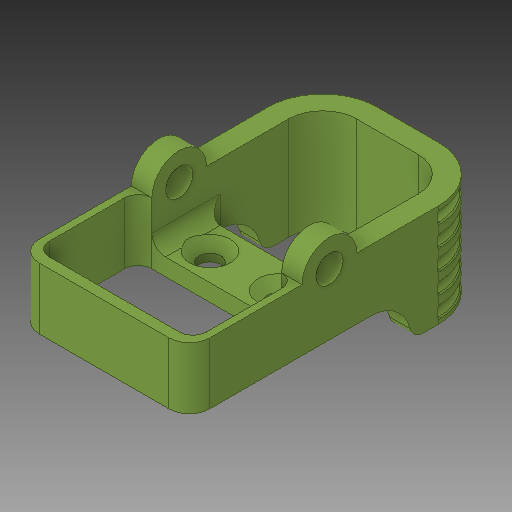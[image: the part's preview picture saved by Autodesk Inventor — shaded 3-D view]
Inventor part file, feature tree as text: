
AUTODESK INVENTOR PART (.ipt)
format: ipt  version: 2018 (Build 220112000, 112)  size: 946,688 bytes
history: native  units: mm
features: sketch x8, extrude x7, fillet x4, plane x2, projected_geometry x2, hole x1, sweep x1, pattern_linear x1
ambient origin geometry x8: Origin, YZ Plane, XZ Plane, XY Plane, X Axis, Y Axis, Z Axis, Center Point
bodies: Solid1 (feature_tree)
feature tree (26):
  extrude  "Extrusion1"  Depth=25.0mm
  extrude  "Extrusion2"  Depth=3.0mm
  sketch  "Sketch3"  dims[d4=15.0mm d5=0.0mm d6=15.0mm]
  extrude  "Extrusion3"  Depth=15.0mm
  extrude  "Extrusion4"  Depth=26.5mm
  extrude  "Extrusion5"  Depth=2.0mm
  hole  "Hole1"  [1 undecoded]
  extrude  "Extrusion6"  Depth=20.5mm
  extrude  "Extrusion7"  Depth=2.0mm
  plane  "Work Plane1"
  sketch  "Sketch7"  dims[d15=4.0mm d17=20.5mm]
  plane  "Work Plane2"
  sweep  "Sweep1"
  pattern_linear  "Rectangular Pattern1"  Spacing1=23.0mm  [1 undecoded]
  fillet  "Fillet1"  Radius=15.0mm
  fillet  "Fillet2"  Radius=1.0mm
  fillet  "Fillet3"  Radius=1.5mm
  fillet  "Fillet4"  Radius=3.0mm
  sketch  "Sketch1"  dims[d0=44.5mm d1=25.0mm]
  sketch  "Sketch2"  dims[d2=8.0mm d3=3.0mm]
  sketch  "Sketch4"  dims[d7=9.0mm d9=26.5mm]
  sketch  "Sketch5"  dims[d10=6.0mm d11=2.0mm]
  sketch  "Sketch6"  dims[d12=15.0mm d13=0.0mm d14=8.0mm]
  sketch  "Sketch8"  dims[d18=3.0mm d19=0.0mm d20=19.0mm d21=17.0mm d22=23.0mm d23=15.0mm d24=1.0mm d25=1.5mm d26=3.0mm d27=3.0mm d28=5.0mm d29=2.0mm d30=15.0mm d31=0.0mm d32=6.5mm d33=0.0mm d34=20.5mm d35=7.5mm d36=10.0mm d37=3.2mm d38=6.0mm d39=6.0mm d40=2.0mm d41=90.0deg d42=5.25mm d43=20.594885mm d44=50.0mm d45=0.0mm d46=3.0mm d47=0.0mm d48=-1.52mm d49=10.75mm d50=1.5mm d51=0.0mm d52=0.0mm d53=50.0mm d55=3.0mm d56=0.2mm d57=0.2mm d58=0.21mm d59=2.0mm]
  projected_geometry  "Project Cut Edges1"
  projected_geometry  "Project Cut Edges2"
note: 2 required parameter values undecoded (feature->parameter linkage not recoverable at this tier; creation-order binding heuristic only, values carry confidence <= 0.55)
